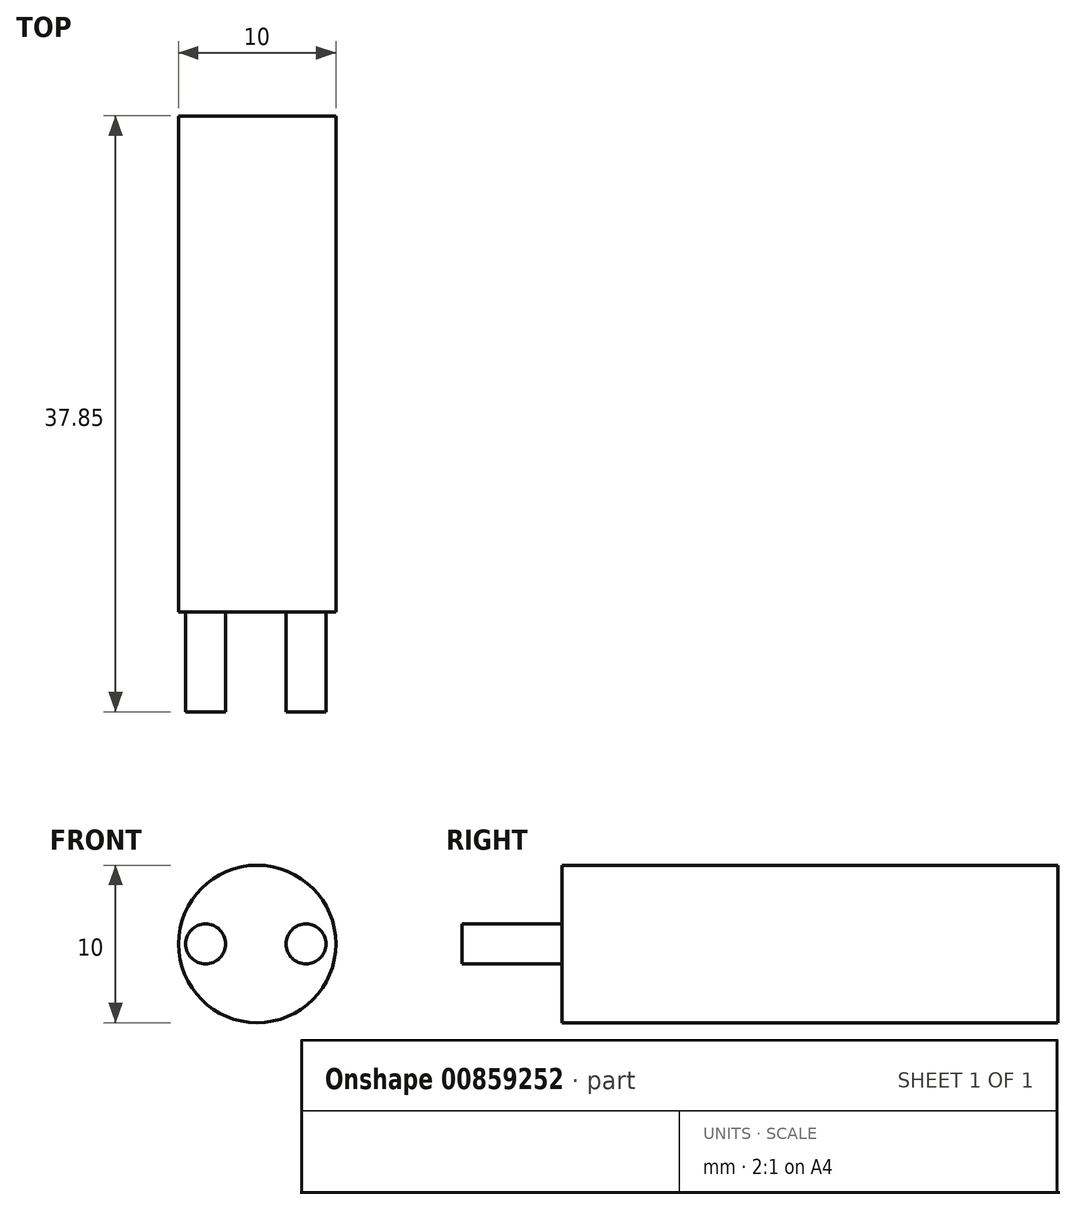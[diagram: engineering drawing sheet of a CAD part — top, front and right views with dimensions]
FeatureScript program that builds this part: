
annotation { "Feature Type Name" : "Feature", "Feature Type Description" : "" }
export const myFeature = defineFeature(function(context is Context, id is Id, definition is map)
    precondition{}
    {
        {
            var Q0;
            Q0=qCreatedBy(makeId("Front.planeOp"),FACE);
            var sketch = newSketch(context, id + "F0", { "sketchPlane" : qUnion([Q0])});
            skCircle(sketch, "E0", {"center": v(0, 0) * mm, "radius": 5 * mm});
            skSolve(sketch);
        }
        {
            var Q0;
            Q0 = qSketchRegion(id + "F0", true);
            extrude(context, id + "F1", {"entities" : qUnion([Q0]), "oppositeDirection" : true, "depth" : 31.5 * mm, "offsetDistance" : 25.4 * mm});
        }
        {
            var Q0;
            Q0=makeQuery(id+"F1.opExtrude","CAP_FACE",FACE,{"disambiguationData":[OSD([sQuery(id+"F0.wireOp",EDGE,"E0")])],"isStart":true});
            var sketch = newSketch(context, id + "F2", { "sketchPlane" : qUnion([Q0])});
            skCircle(sketch, "E1", {"center": v(-3.27, 0) * mm, "radius": 1.27 * mm});
            skCircle(sketch, "E2", {"center": v(3.1, 0) * mm, "radius": 1.27 * mm});
            skSolve(sketch);
        }
        {
            var Q0;
            Q0 = qSketchRegion(id + "F2", true);
            extrude(context, id + "F3", {"entities" : qUnion([Q0]), "operationType" : NewBodyOperationType.ADD, "depth" : 6.35 * mm, "offsetDistance" : 25.4 * mm});
        }
    });
